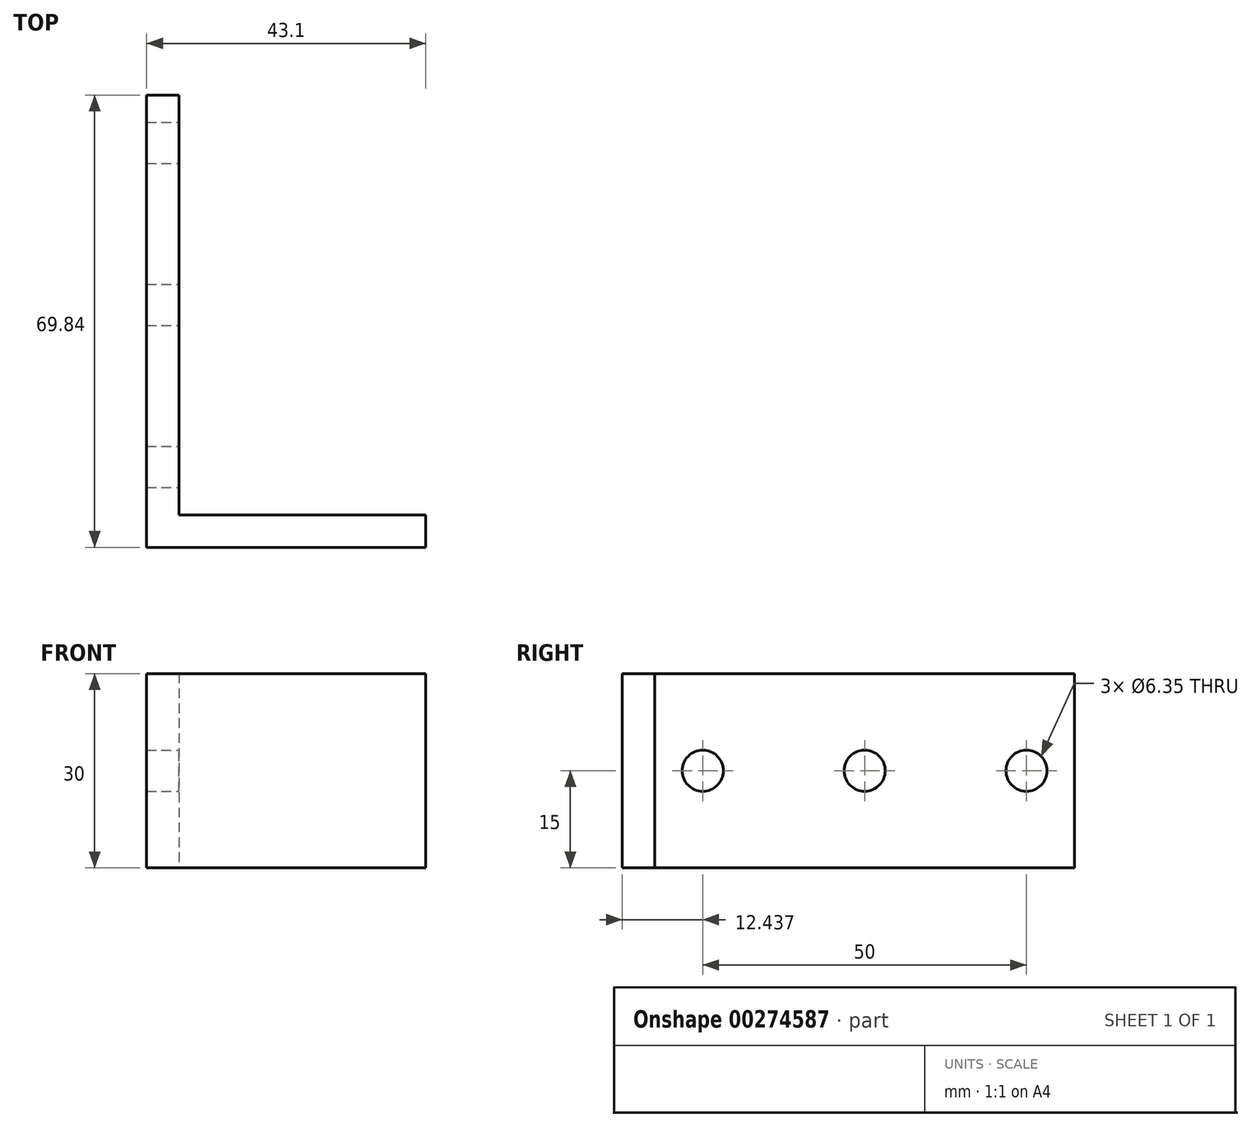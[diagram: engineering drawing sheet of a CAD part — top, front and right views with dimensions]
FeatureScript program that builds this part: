
annotation { "Feature Type Name" : "Feature", "Feature Type Description" : "" }
export const myFeature = defineFeature(function(context is Context, id is Id, definition is map)
    precondition{}
    {
        {
            var Q0;
            Q0=qCreatedBy(makeId("Top.planeOp"),FACE);
            var sketch = newSketch(context, id + "F0", { "sketchPlane" : qUnion([Q0])});
            skLineSegment(sketch, "E0.bottom", {"start": v(2.5, -34.92) * mm, "end": v(-2.5, -34.92) * mm});
            skLineSegment(sketch, "E0.top", {"start": v(2.5, 34.93) * mm, "end": v(-2.5, 34.93) * mm});
            skLineSegment(sketch, "E0.left", {"start": v(2.5, -34.92) * mm, "end": v(2.5, 34.93) * mm});
            skLineSegment(sketch, "E0.right", {"start": v(-2.5, -34.92) * mm, "end": v(-2.5, 34.93) * mm});
            skPoint(sketch, "E0.middle", {"position": v(0, 0) * mm});
            skLineSegment(sketch, "E1.bottom", {"start": v(2.5, -34.92) * mm, "end": v(40.6, -34.92) * mm});
            skLineSegment(sketch, "E1.top", {"start": v(2.5, -29.93) * mm, "end": v(40.6, -29.92) * mm});
            skLineSegment(sketch, "E1.left", {"start": v(2.5, -34.92) * mm, "end": v(2.5, -29.93) * mm});
            skLineSegment(sketch, "E1.right", {"start": v(40.6, -34.92) * mm, "end": v(40.6, -29.92) * mm});
            skSolve(sketch);
        }
        {
            var Q0;
            Q0 = qSketchRegion(id + "F0", true);
            extrude(context, id + "F1", {"entities" : qUnion([Q0]), "depth" : 30 * mm});
        }
        {
            var Q0;
            Q0=makeQuery(id+"F1.opExtrude","SWEPT_FACE",FACE,{"disambiguationData":[OSD([sQuery(id+"F0.wireOp",EDGE,"E0.left")])]});
            var sketch = newSketch(context, id + "F2", { "sketchPlane" : qUnion([Q0])});
            skCircle(sketch, "E2", {"center": v(-22.48, 15) * mm, "radius": 3.18 * mm});
            skCircle(sketch, "E3.1.0.0", {"center": v(2.52, 15) * mm, "radius": 3.18 * mm});
            skCircle(sketch, "E3.2.0.0", {"center": v(27.52, 15) * mm, "radius": 3.18 * mm});
            skLineSegment(sketch, "E3.direction1", {"start": v(-22.48, 15) * mm, "end": v(2.52, 15) * mm, "construction": true});
            skSolve(sketch);
        }
        {
            var Q0;
            Q0 = qSketchRegion(id + "F2", true);
            extrude(context, id + "F3", {"entities" : qUnion([Q0]), "operationType" : NewBodyOperationType.REMOVE, "oppositeDirection" : true, "depth" : 25.4 * mm});
        }
    });
